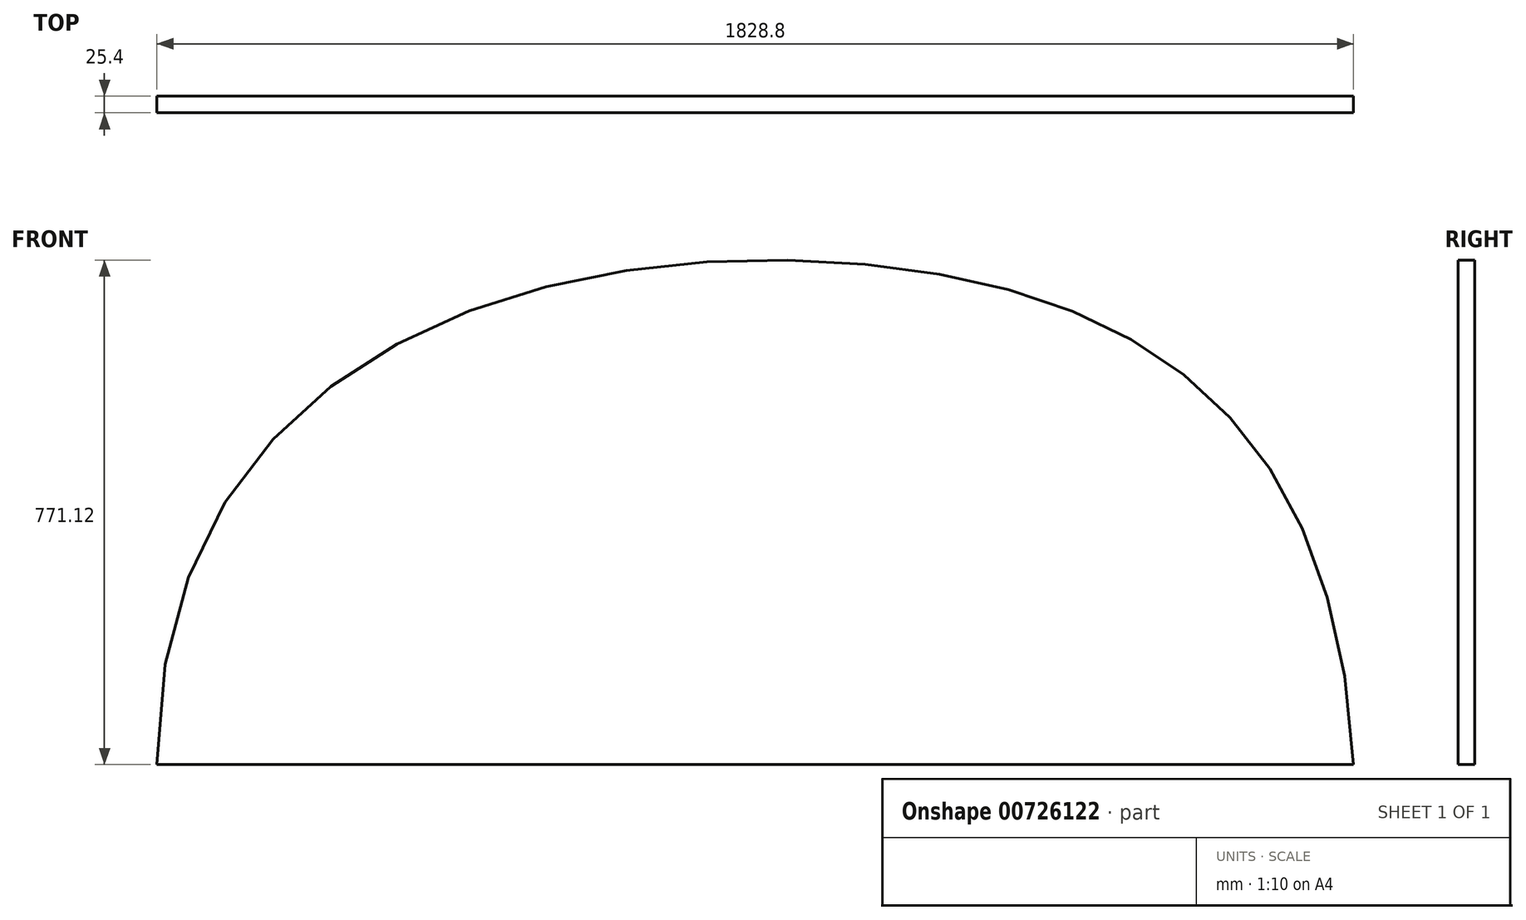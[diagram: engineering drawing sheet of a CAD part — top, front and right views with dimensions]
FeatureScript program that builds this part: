
annotation { "Feature Type Name" : "Feature", "Feature Type Description" : "" }
export const myFeature = defineFeature(function(context is Context, id is Id, definition is map)
    precondition{}
    {
        {
            var Q0;
            Q0=qCreatedBy(makeId("Front.planeOp"),FACE);
            var sketch = newSketch(context, id + "F0", { "sketchPlane" : qUnion([Q0])});
            skFitSpline(sketch, "E0", {"points": [v(-1294.94, -78.74) * mm, v(-188.05, 683.26) * mm, v(533.86, -78.74) * mm], "startDerivative": vector(2.84, 3746.86) * mm, "endDerivative": vector(166.09, -3294.48) * mm});
            skLineSegment(sketch, "E1", {"start": v(-1294.94, -78.74) * mm, "end": v(533.86, -78.74) * mm});
            skSolve(sketch);
        }
        {
            var Q0;
            Q0 = qSketchRegion(id + "F0", true);
            extrude(context, id + "F1", {"entities" : qUnion([Q0]), "depth" : 25.4 * mm, "offsetDistance" : 25.4 * mm});
        }
    });
